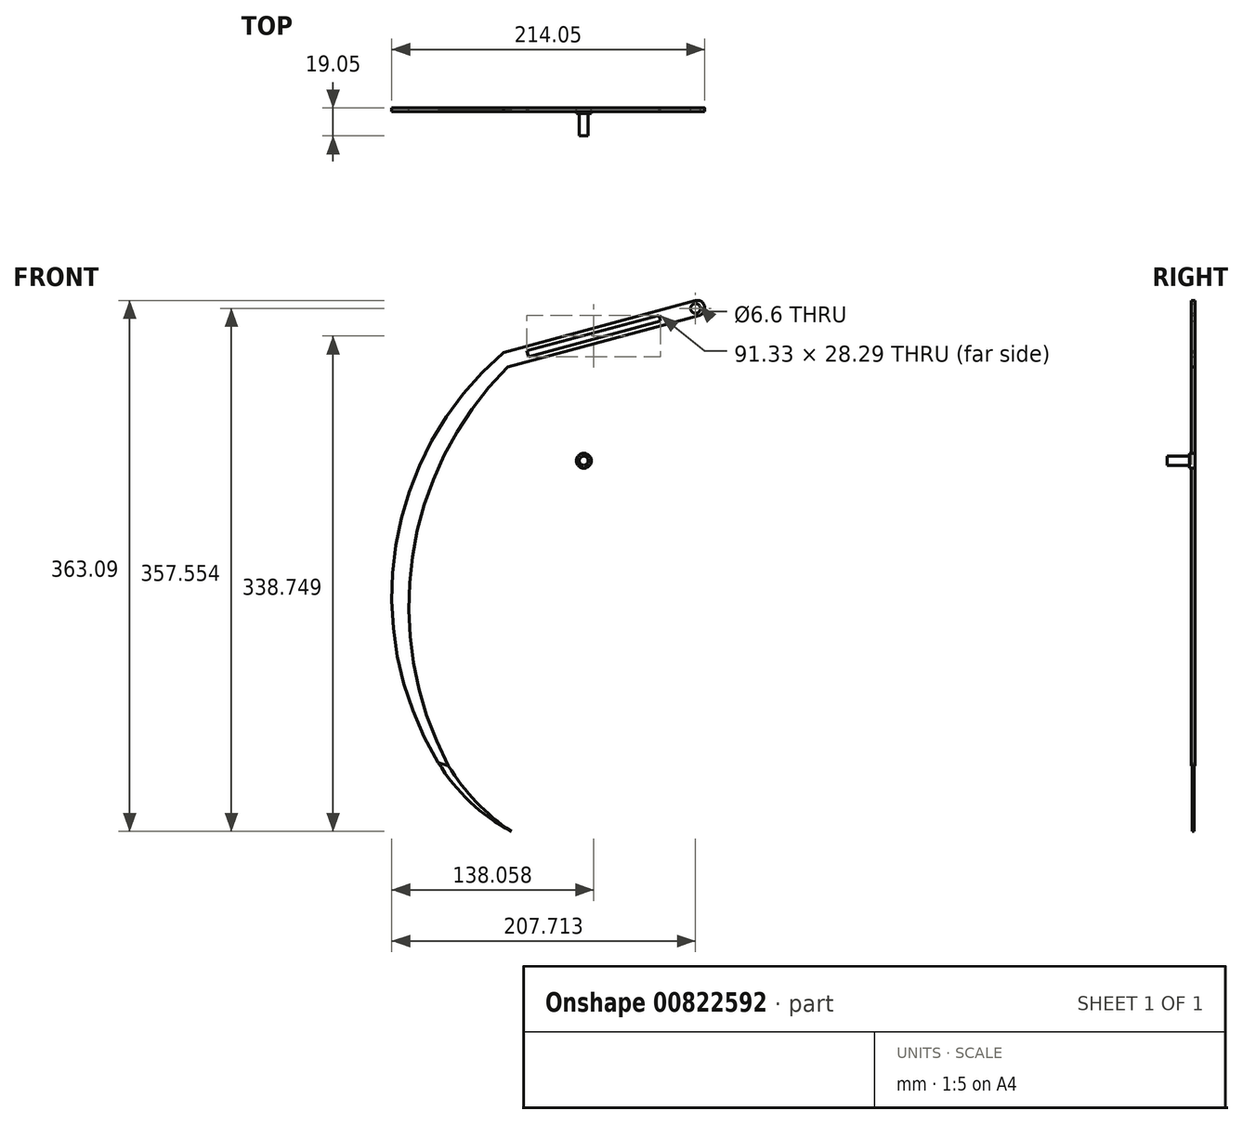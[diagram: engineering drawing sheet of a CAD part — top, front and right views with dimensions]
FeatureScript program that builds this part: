
annotation { "Feature Type Name" : "Feature", "Feature Type Description" : "" }
export const myFeature = defineFeature(function(context is Context, id is Id, definition is map)
    precondition{}
    {
        {
            var Q0;
            Q0=qCreatedBy(makeId("Front.planeOp"),FACE);
            var sketch = newSketch(context, id + "F0", { "sketchPlane" : qUnion([Q0])});
            skLineSegment(sketch, "E0", {"start": v(114.4, 140.2) * mm, "end": v(-16.66, 104.82) * mm});
            skLineSegment(sketch, "E1", {"start": v(-16.66, 104.82) * mm, "end": v(-13.94, 94.77) * mm});
            skLineSegment(sketch, "E2", {"start": v(-13.94, 94.77) * mm, "end": v(117.12, 130.14) * mm});
            skLineSegment(sketch, "E3", {"start": v(120.7, 136.37) * mm, "end": v(120.63, 136.62) * mm});
            skLineSegment(sketch, "E4", {"start": v(0.27, 101.9) * mm, "end": v(90.54, 126.26) * mm});
            skLineSegment(sketch, "E5", {"start": v(89.48, 130.18) * mm, "end": v(90.54, 126.26) * mm});
            skLineSegment(sketch, "E6", {"start": v(89.48, 130.18) * mm, "end": v(-0.79, 105.82) * mm});
            skLineSegment(sketch, "E7", {"start": v(0.27, 101.9) * mm, "end": v(-0.79, 105.82) * mm});
            skArc(sketch, "E8", {"start": v(-16.66, 104.82) * mm, "mid": v(-90.44, -27.19) * mm, "end": v(-61.38, -175.6) * mm});
            skArc(sketch, "E9", {"start": v(-13.94, 94.77) * mm, "mid": v(-79.02, -34.9) * mm, "end": v(-54.35, -177.88) * mm});
            skLineSegment(sketch, "E10", {"start": v(-61.38, -175.6) * mm, "end": v(-54.35, -177.88) * mm});
            skArc(sketch, "E11", {"start": v(-61.38, -175.6) * mm, "mid": v(-39.62, -202.53) * mm, "end": v(-11.48, -222.71) * mm});
            skArc(sketch, "E12", {"start": v(-54.35, -177.88) * mm, "mid": v(-35.37, -202.64) * mm, "end": v(-11.48, -222.71) * mm});
            skCircle(sketch, "E13", {"center": v(114.53, 134.84) * mm, "radius": 3.3 * mm});
            skPoint(sketch, "E14.visualSharp", {"position": v(119.3, 141.53) * mm});
            skArc(sketch, "E14.filletArc", {"start": v(120.63, 136.62) * mm, "mid": v(118.26, 139.7) * mm, "end": v(114.4, 140.2) * mm});
            skPoint(sketch, "E15.visualSharp", {"position": v(122.02, 131.47) * mm});
            skArc(sketch, "E15.filletArc", {"start": v(117.12, 130.14) * mm, "mid": v(120.2, 132.52) * mm, "end": v(120.7, 136.37) * mm});
            skLineSegment(sketch, "E16", {"start": v(77.93, 122.86) * mm, "end": v(78.76, 119.8) * mm, "construction": true});
            skLineSegment(sketch, "E17", {"start": v(76.66, 126.72) * mm, "end": v(75.83, 129.8) * mm, "construction": true});
            skSolve(sketch);
        }
        {
            var Q0;
            Q0=makeQuery(id+"F0.imprint","IMPRINT",FACE,{"disambiguationData":[TD([[makeQuery(id+"F0.imprint","IMPRINT",EDGE,{"derivedFrom":sQuery(id+"F0.wireOp",EDGE,"E0")}),1.0]])]});
            var Q1;
            Q1=makeQuery(id+"F0.imprint","IMPRINT",FACE,{"disambiguationData":[TD([[makeQuery(id+"F0.imprint","IMPRINT",EDGE,{"derivedFrom":sQuery(id+"F0.wireOp",EDGE,"E1")}),-1.0]])]});
            extrude(context, id + "F1", {"entities" : qUnion([Q0, Q1]), "depth" : 2.54 * mm, "offsetDistance" : 25.4 * mm});
        }
        {
            var Q0;
            {var subQ2=sQuery(id+"F0.wireOp",EDGE,"E11");Q0=makeQuery(id+"F0.imprint","IMPRINT",FACE,{"disambiguationData":[TD([[makeQuery(id+"F0.imprint","IMPRINT",EDGE,{"derivedFrom":subQ2}),1.0]])]});}
            extrude(context, id + "F2", {"entities" : qUnion([Q0]), "operationType" : NewBodyOperationType.ADD, "depth" : 1.9 * mm, "offsetDistance" : 25.4 * mm, "hasSecondDirection" : true, "secondDirectionOppositeDirection" : false, "secondDirectionDepth" : 0.64 * mm});
        }
        {
            var Q0;
            Q0=qCreatedBy(makeId("Front.planeOp"),FACE);
            var sketch = newSketch(context, id + "F3", { "sketchPlane" : qUnion([Q0])});
            skCircle(sketch, "E18", {"center": v(38.15, 30.73) * mm, "radius": 3.05 * mm});
            skCircle(sketch, "E19", {"center": v(38.15, 30.73) * mm, "radius": 5.08 * mm});
            skSolve(sketch);
        }
        {
            var Q0;
            Q0=makeQuery(id+"F3.imprint","IMPRINT",FACE,{"disambiguationData":[TD([[makeQuery(id+"F3.imprint","IMPRINT",EDGE,{"derivedFrom":sQuery(id+"F3.wireOp",EDGE,"E18")}),1.0]])]});
            extrude(context, id + "F4", {"entities" : qUnion([Q0]), "depth" : 19.05 * mm, "offsetDistance" : 25.4 * mm});
        }
        {
            var Q0;
            Q0=makeQuery(id+"F3.imprint","IMPRINT",FACE,{"disambiguationData":[TD([[makeQuery(id+"F3.imprint","IMPRINT",EDGE,{"derivedFrom":sQuery(id+"F3.wireOp",EDGE,"E18")}),-1.0]])]});
            extrude(context, id + "F5", {"entities" : qUnion([Q0]), "operationType" : NewBodyOperationType.ADD, "depth" : 3.8 * mm, "offsetDistance" : 25.4 * mm});
        }
    });
